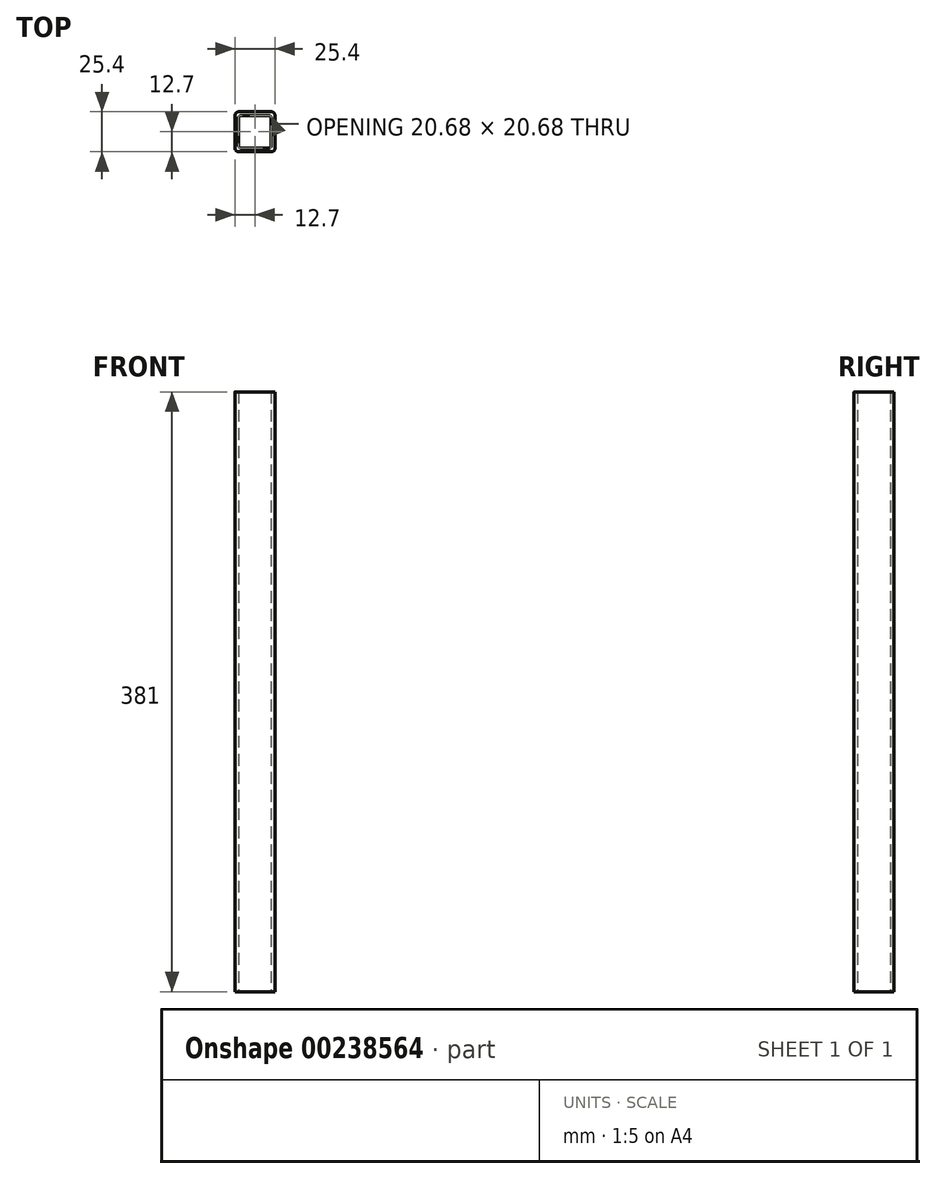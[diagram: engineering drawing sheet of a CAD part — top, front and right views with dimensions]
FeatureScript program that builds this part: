
annotation { "Feature Type Name" : "Feature", "Feature Type Description" : "" }
export const myFeature = defineFeature(function(context is Context, id is Id, definition is map)
    precondition{}
    {
        {
            var Q0;
            Q0=qCreatedBy(makeId("Top.planeOp"),FACE);
            var sketch = newSketch(context, id + "F0", { "sketchPlane" : qUnion([Q0])});
            skLineSegment(sketch, "E0", {"start": v(-12.7, 10.34) * mm, "end": v(-12.7, -10.34) * mm});
            skLineSegment(sketch, "E1", {"start": v(-10.34, -12.7) * mm, "end": v(10.34, -12.7) * mm});
            skLineSegment(sketch, "E2", {"start": v(12.7, -10.34) * mm, "end": v(12.7, 10.34) * mm});
            skLineSegment(sketch, "E3", {"start": v(10.34, 12.7) * mm, "end": v(-10.34, 12.7) * mm});
            skLineSegment(sketch, "E4", {"start": v(0, 12.7) * mm, "end": v(0, -12.7) * mm, "construction": true});
            skLineSegment(sketch, "E5", {"start": v(-12.7, 0) * mm, "end": v(12.7, 0) * mm, "construction": true});
            skPoint(sketch, "E6", {"position": v(0, 0) * mm});
            skPoint(sketch, "E7.visualSharp", {"position": v(-12.7, 12.7) * mm});
            skArc(sketch, "E7.filletArc", {"start": v(-10.34, 12.7) * mm, "mid": v(-12, 12) * mm, "end": v(-12.7, 10.34) * mm});
            skPoint(sketch, "E8.visualSharp", {"position": v(12.7, 12.7) * mm});
            skArc(sketch, "E8.filletArc", {"start": v(12.7, 10.34) * mm, "mid": v(12, 12) * mm, "end": v(10.34, 12.7) * mm});
            skPoint(sketch, "E9.visualSharp", {"position": v(12.7, -12.7) * mm});
            skArc(sketch, "E9.filletArc", {"start": v(10.34, -12.7) * mm, "mid": v(12, -12) * mm, "end": v(12.7, -10.34) * mm});
            skPoint(sketch, "E10.visualSharp", {"position": v(-12.7, -12.7) * mm});
            skArc(sketch, "E10.filletArc", {"start": v(-12.7, -10.34) * mm, "mid": v(-12, -12) * mm, "end": v(-10.34, -12.7) * mm});
            skLineSegment(sketch, "E11.0", {"start": v(8.81, 10.34) * mm, "end": v(-8.81, 10.34) * mm});
            skLineSegment(sketch, "E12.0", {"start": v(10.34, -8.81) * mm, "end": v(10.34, 8.81) * mm});
            skLineSegment(sketch, "E13.0", {"start": v(-8.81, -10.34) * mm, "end": v(8.81, -10.34) * mm});
            skLineSegment(sketch, "E14.0", {"start": v(-10.34, 8.81) * mm, "end": v(-10.34, -8.81) * mm});
            skArc(sketch, "E15.filletArc", {"start": v(-8.81, 10.34) * mm, "mid": v(-9.9, 9.9) * mm, "end": v(-10.34, 8.81) * mm});
            skArc(sketch, "E16.filletArc", {"start": v(10.34, 8.81) * mm, "mid": v(9.9, 9.9) * mm, "end": v(8.81, 10.34) * mm});
            skArc(sketch, "E17.filletArc", {"start": v(8.81, -10.34) * mm, "mid": v(9.9, -9.9) * mm, "end": v(10.34, -8.81) * mm});
            skArc(sketch, "E18.filletArc", {"start": v(-10.34, -8.81) * mm, "mid": v(-9.9, -9.9) * mm, "end": v(-8.81, -10.34) * mm});
            skSolve(sketch);
        }
        {
            var Q0;
            Q0=makeQuery(id+"F0.imprint","IMPRINT",FACE,{"disambiguationData":[TD([[makeQuery(id+"F0.imprint","IMPRINT",EDGE,{"derivedFrom":sQuery(id+"F0.wireOp",EDGE,"E0")}),1.0]])]});
            extrude(context, id + "F1", {"entities" : qUnion([Q0]), "depth" : 381 * mm});
        }
    });
